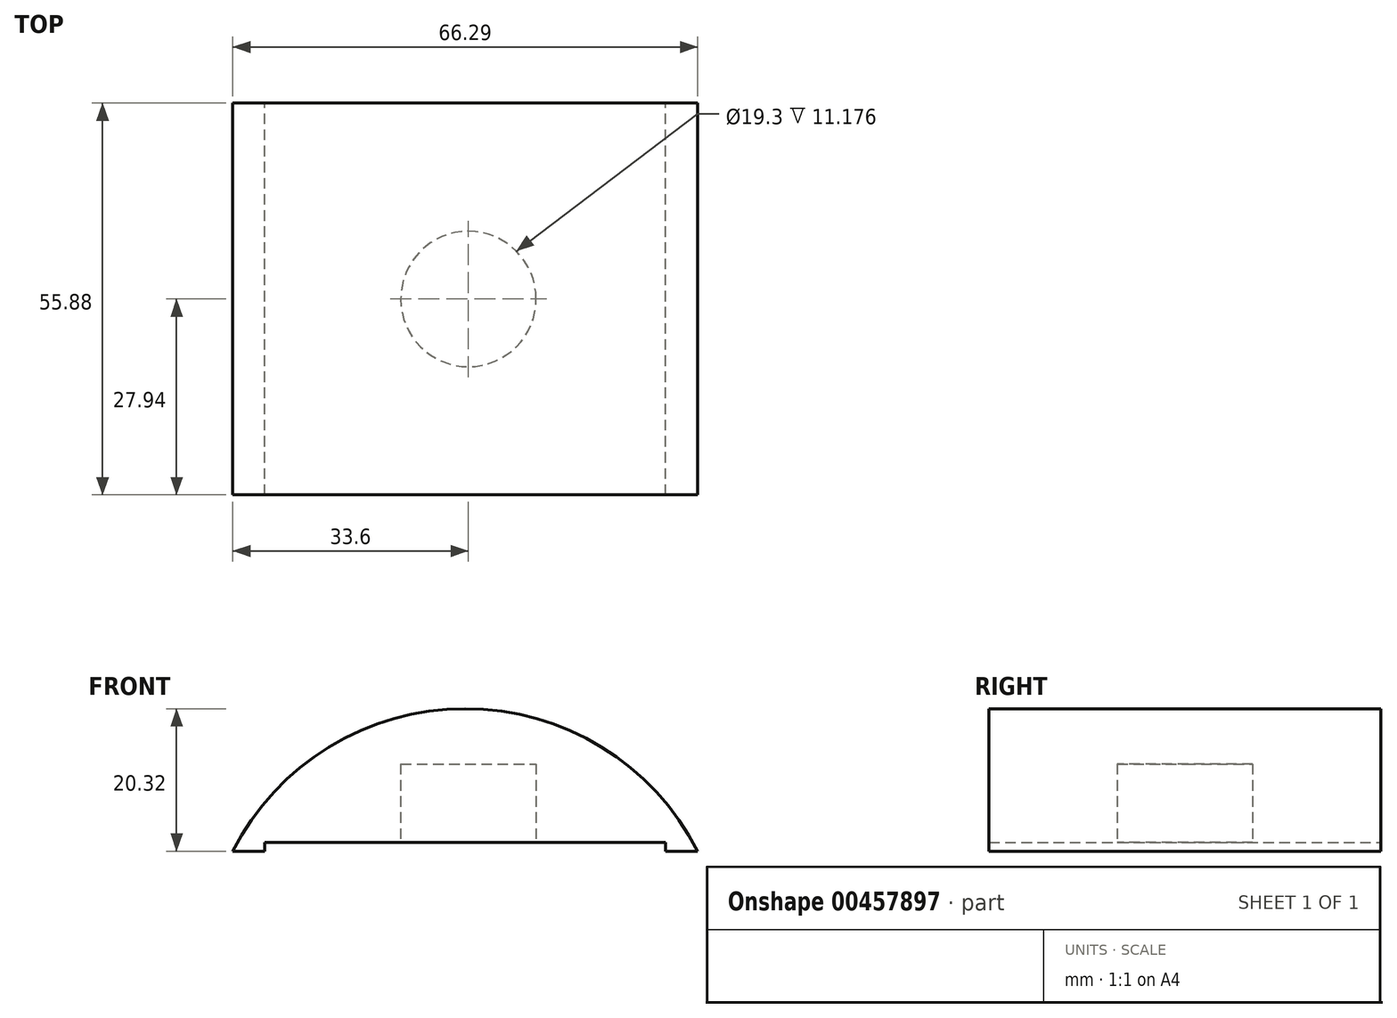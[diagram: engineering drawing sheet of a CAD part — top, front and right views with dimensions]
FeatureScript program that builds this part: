
annotation { "Feature Type Name" : "Feature", "Feature Type Description" : "" }
export const myFeature = defineFeature(function(context is Context, id is Id, definition is map)
    precondition{}
    {
        {
            var Q0;
            Q0=qCreatedBy(makeId("Front.planeOp"),FACE);
            var sketch = newSketch(context, id + "F0", { "sketchPlane" : qUnion([Q0])});
            skArc(sketch, "E0", {"start": v(32.7, 0) * mm, "mid": v(-0.45, 20.32) * mm, "end": v(-33.6, 0) * mm});
            skLineSegment(sketch, "E1", {"start": v(-33.6, 0) * mm, "end": v(32.7, 0) * mm});
            skSolve(sketch);
        }
        {
            var Q0;
            Q0 = qSketchRegion(id + "F0", true);
            extrude(context, id + "F1", {"entities" : qUnion([Q0]), "depth" : 55.88 * mm});
        }
        {
            var Q0;
            Q0=makeQuery(id+"F1.opExtrude","SWEPT_FACE",FACE,{"disambiguationData":[OSD([sQuery(id+"F0.wireOp",EDGE,"E1")])]});
            var sketch = newSketch(context, id + "F2", { "sketchPlane" : qUnion([Q0])});
            skLineSegment(sketch, "E2", {"start": v(-33.6, 55.88) * mm, "end": v(-29.03, 55.88) * mm});
            skLineSegment(sketch, "E3", {"start": v(-29.03, 55.88) * mm, "end": v(-29.03, 0) * mm});
            skLineSegment(sketch, "E4", {"start": v(-29.03, 0) * mm, "end": v(-33.6, 0) * mm});
            skLineSegment(sketch, "E5", {"start": v(-33.6, 0) * mm, "end": v(-33.6, 55.88) * mm});
            skLineSegment(sketch, "E6", {"start": v(32.7, 55.88) * mm, "end": v(28.12, 55.88) * mm});
            skLineSegment(sketch, "E7", {"start": v(28.12, 55.88) * mm, "end": v(28.12, 0) * mm});
            skLineSegment(sketch, "E8", {"start": v(28.12, 0) * mm, "end": v(32.7, 0) * mm});
            skLineSegment(sketch, "E9", {"start": v(32.7, 0) * mm, "end": v(32.7, 55.88) * mm});
            skPoint(sketch, "E10.startSnap0", {"position": v(-0.45, 55.88) * mm});
            skCircle(sketch, "E11", {"center": v(0, 27.94) * mm, "radius": 9.65 * mm});
            skSolve(sketch);
        }
        {
            var Q0;
            Q0=makeQuery(id+"F2.imprint","IMPRINT",FACE,{"disambiguationData":[TD([[makeQuery(id+"F2.imprint","IMPRINT",EDGE,{"derivedFrom":sQuery(id+"F2.wireOp",EDGE,"E11")}),1.0]])]});
            extrude(context, id + "F3", {"entities" : qUnion([Q0]), "operationType" : NewBodyOperationType.REMOVE, "oppositeDirection" : true, "depth" : 12.45 * mm});
        }
        {
            var Q0;
            Q0=makeQuery(id+"F1.opExtrude","SWEPT_FACE",FACE,{"disambiguationData":[OSD([sQuery(id+"F0.wireOp",EDGE,"E1")])]});
            var sketch = newSketch(context, id + "F4", { "sketchPlane" : qUnion([Q0])});
            skLineSegment(sketch, "E12", {"start": v(-29.03, 55.88) * mm, "end": v(-29.03, 0) * mm});
            skLineSegment(sketch, "E13", {"start": v(28.12, 55.88) * mm, "end": v(28.12, 0) * mm});
            skLineSegment(sketch, "E14", {"start": v(-33.6, 55.88) * mm, "end": v(-29.03, 55.88) * mm});
            skLineSegment(sketch, "E15", {"start": v(-33.6, 55.88) * mm, "end": v(-33.6, 0) * mm});
            skLineSegment(sketch, "E16", {"start": v(-33.6, 0) * mm, "end": v(-29.03, 0) * mm});
            skLineSegment(sketch, "E17", {"start": v(28.12, 55.88) * mm, "end": v(32.7, 55.88) * mm});
            skLineSegment(sketch, "E18", {"start": v(32.7, 55.88) * mm, "end": v(32.7, 0) * mm});
            skLineSegment(sketch, "E19", {"start": v(32.7, 0) * mm, "end": v(28.12, 0) * mm});
            skLineSegment(sketch, "E20", {"start": v(-29.03, 55.88) * mm, "end": v(28.12, 55.88) * mm});
            skLineSegment(sketch, "E21", {"start": v(-29.03, 0) * mm, "end": v(28.12, 0) * mm});
            skSolve(sketch);
        }
        {
            var Q0;
            Q0=makeQuery(id+"F4.imprint","IMPRINT",FACE,{"disambiguationData":[TD([[makeQuery(id+"F4.imprint","IMPRINT",EDGE,{"derivedFrom":sQuery(id+"F4.wireOp",EDGE,"E12")}),1.0]])]});
            extrude(context, id + "F5", {"entities" : qUnion([Q0]), "operationType" : NewBodyOperationType.REMOVE, "oppositeDirection" : true, "depth" : 1.27 * mm});
        }
    });
